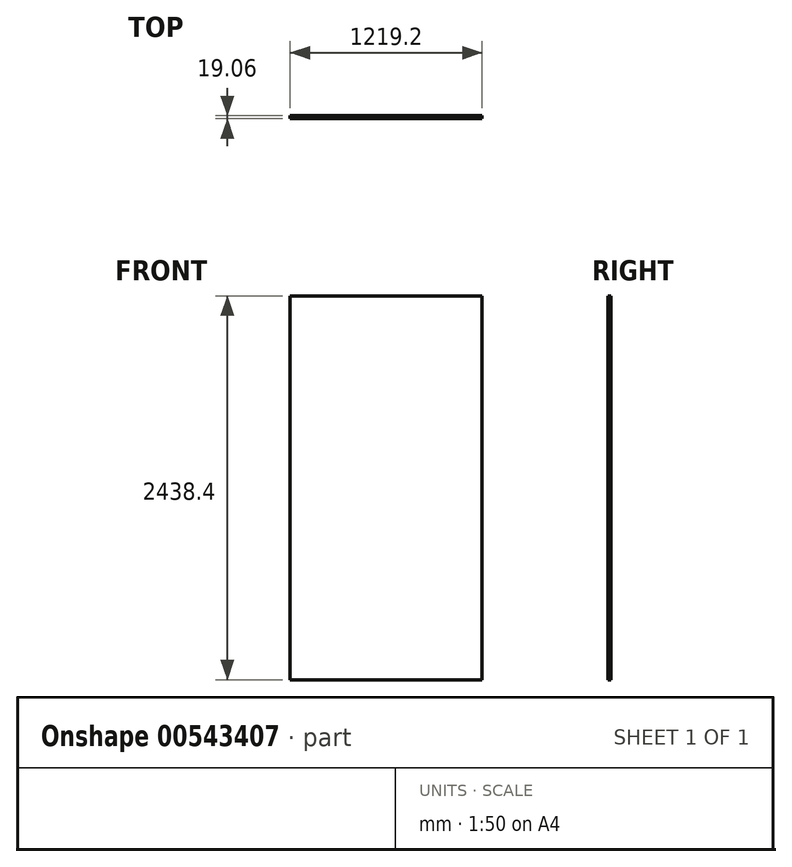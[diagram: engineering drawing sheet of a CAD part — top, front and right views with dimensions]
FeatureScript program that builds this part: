
annotation { "Feature Type Name" : "Feature", "Feature Type Description" : "" }
export const myFeature = defineFeature(function(context is Context, id is Id, definition is map)
    precondition{}
    {
        {
            var Q0;
            Q0=qCreatedBy(makeId("Front.planeOp"),FACE);
            var sketch = newSketch(context, id + "F0", { "sketchPlane" : qUnion([Q0])});
            skLineSegment(sketch, "E0.bottom", {"start": v(-609.6, 1219.2) * mm, "end": v(609.6, 1219.2) * mm});
            skLineSegment(sketch, "E0.top", {"start": v(-609.6, -1219.2) * mm, "end": v(609.6, -1219.2) * mm});
            skLineSegment(sketch, "E0.left", {"start": v(-609.6, 1219.2) * mm, "end": v(-609.6, -1219.2) * mm});
            skLineSegment(sketch, "E0.right", {"start": v(609.6, 1219.2) * mm, "end": v(609.6, -1219.2) * mm});
            skPoint(sketch, "E0.middle", {"position": v(0, 0) * mm});
            skSolve(sketch);
        }
        {
            var Q0;
            Q0 = qSketchRegion(id + "F0", true);
            extrude(context, id + "F1", {"entities" : qUnion([Q0]), "endBound" : BoundingType.SYMMETRIC, "depth" : 19.05 * mm, "offsetDistance" : 25.4 * mm});
        }
    });
